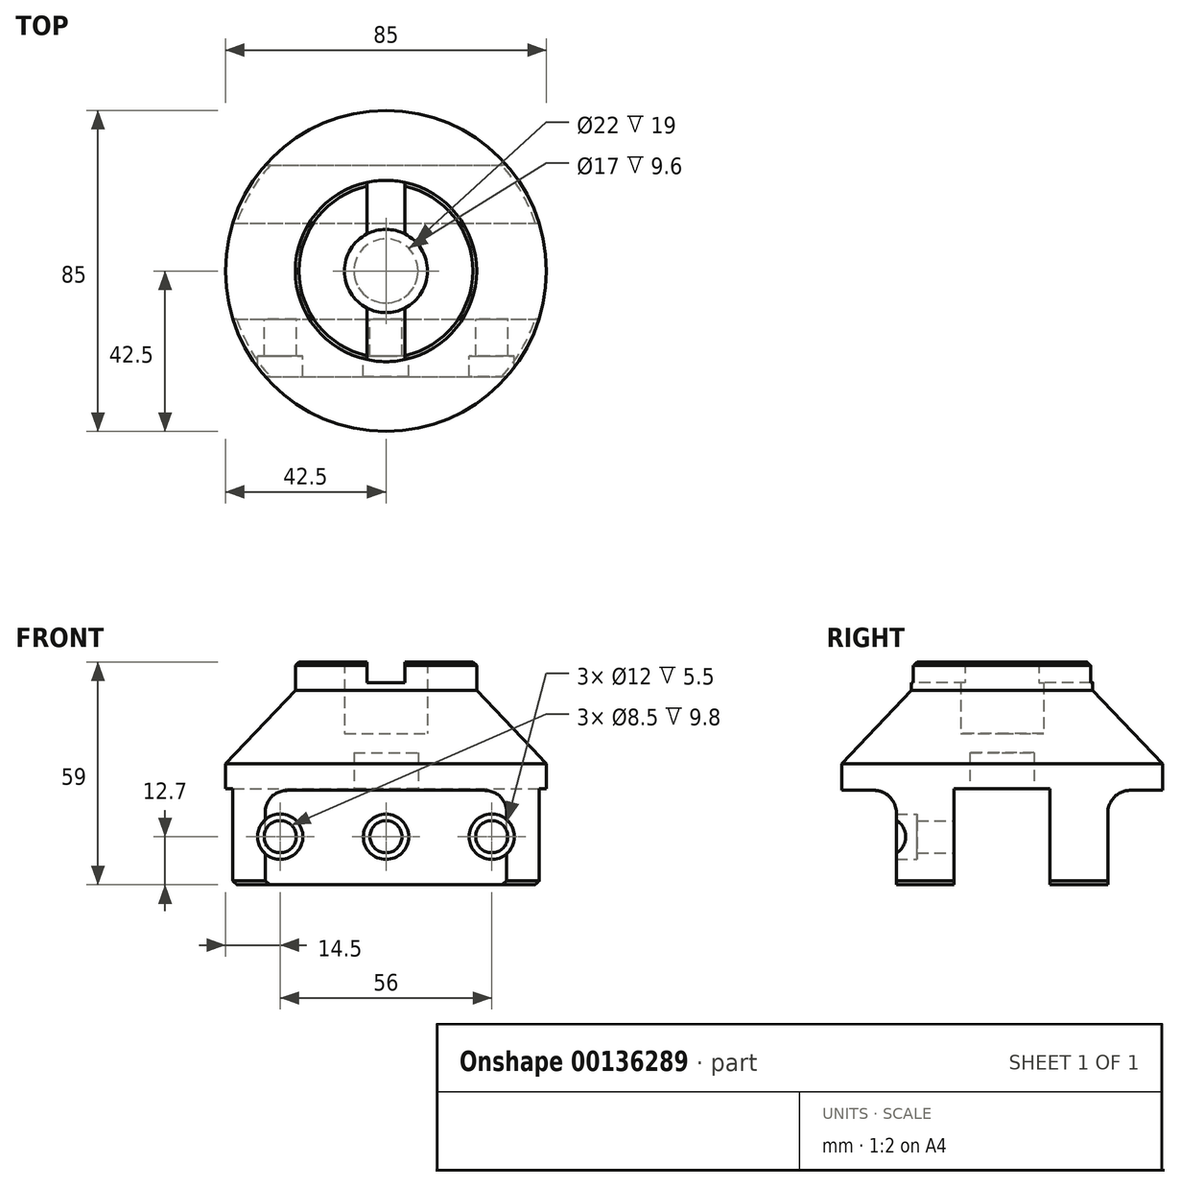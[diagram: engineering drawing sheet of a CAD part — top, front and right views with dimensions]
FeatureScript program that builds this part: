
annotation { "Feature Type Name" : "Feature", "Feature Type Description" : "" }
export const myFeature = defineFeature(function(context is Context, id is Id, definition is map)
    precondition{}
    {
        {
            var Q0;
            Q0=qCreatedBy(makeId("Front.planeOp"),FACE);
            var sketch = newSketch(context, id + "F0", { "sketchPlane" : qUnion([Q0])});
            skLineSegment(sketch, "E0", {"start": v(0, 0) * mm, "end": v(42.5, 0) * mm});
            skLineSegment(sketch, "E1", {"start": v(42.5, 0) * mm, "end": v(42.5, 32) * mm});
            skLineSegment(sketch, "E2", {"start": v(42.5, 32) * mm, "end": v(24, 51.5) * mm});
            skLineSegment(sketch, "E3", {"start": v(24, 51.5) * mm, "end": v(24, 59) * mm});
            skLineSegment(sketch, "E4", {"start": v(24, 59) * mm, "end": v(0, 59) * mm});
            skLineSegment(sketch, "E5", {"start": v(0, 59) * mm, "end": v(0, 0) * mm});
            skSolve(sketch);
        }
        {
            var Q0;
            Q0=makeQuery(id+"F0.imprint","IMPRINT",FACE,{"disambiguationData":[TD([[makeQuery(id+"F0.imprint","IMPRINT",EDGE,{"derivedFrom":sQuery(id+"F0.wireOp",EDGE,"E0")}),1.0]])]});
            var Q1;
            Q1=sQuery(id+"F0.wireOp",EDGE,"E5");
            revolve(context, id + "F1", {"entities" : qUnion([Q0]), "axis" : qUnion([Q1]), "revolveType" : RevolveType.FULL});
        }
        {
            var Q0;
            Q0=qCreatedBy(makeId("Front.planeOp"),FACE);
            var sketch = newSketch(context, id + "F2", { "sketchPlane" : qUnion([Q0])});
            skLineSegment(sketch, "E6.bottom", {"start": v(0, 59) * mm, "end": v(11, 59) * mm});
            skLineSegment(sketch, "E6.top", {"start": v(0, 40) * mm, "end": v(11, 40) * mm});
            skLineSegment(sketch, "E6.left", {"start": v(0, 59) * mm, "end": v(0, 40) * mm});
            skLineSegment(sketch, "E6.right", {"start": v(11, 59) * mm, "end": v(11, 40) * mm});
            skPoint(sketch, "E7.oppositeSnap0", {"position": v(5.5, 40) * mm});
            skLineSegment(sketch, "E7.bottom", {"start": v(0, 40) * mm, "end": v(5.5, 40) * mm});
            skLineSegment(sketch, "E7.top", {"start": v(0, 35) * mm, "end": v(5.5, 35) * mm});
            skLineSegment(sketch, "E7.left", {"start": v(0, 40) * mm, "end": v(0, 35) * mm});
            skLineSegment(sketch, "E7.right", {"start": v(5.5, 40) * mm, "end": v(5.5, 35) * mm});
            skLineSegment(sketch, "E8.bottom", {"start": v(0, 35) * mm, "end": v(8.5, 35) * mm});
            skLineSegment(sketch, "E8.top", {"start": v(0, 25) * mm, "end": v(8.5, 25) * mm});
            skLineSegment(sketch, "E8.left", {"start": v(0, 35) * mm, "end": v(0, 25) * mm});
            skLineSegment(sketch, "E8.right", {"start": v(8.5, 35) * mm, "end": v(8.5, 25) * mm});
            skSolve(sketch);
        }
        {
            var Q0;
            Q0=makeQuery(id+"F2.imprint","IMPRINT",FACE,{"disambiguationData":[TD([[makeQuery(id+"F2.imprint","IMPRINT",EDGE,{"derivedFrom":sQuery(id+"F2.wireOp",EDGE,"E8.top")}),1.0]])]});
            var Q1;
            Q1=makeQuery(id+"F2.imprint","IMPRINT",FACE,{"disambiguationData":[TD([[makeQuery(id+"F2.imprint","IMPRINT",EDGE,{"derivedFrom":sQuery(id+"F2.wireOp",EDGE,"E7.bottom")}),-1.0]])]});
            var Q2;
            Q2=makeQuery(id+"F2.imprint","IMPRINT",FACE,{"disambiguationData":[TD([[makeQuery(id+"F2.imprint","IMPRINT",EDGE,{"derivedFrom":sQuery(id+"F2.wireOp",EDGE,"E6.bottom")}),-1.0]])]});
            var Q3;
            Q3=sQuery(id+"F2.wireOp",EDGE,"E8.left");
            revolve(context, id + "F3", {"operationType" : NewBodyOperationType.REMOVE, "entities" : qUnion([Q0, Q1, Q2]), "axis" : qUnion([Q3]), "revolveType" : RevolveType.FULL, "oppositeDirection" : true});
        }
        {
            var Q0;
            Q0=qCreatedBy(makeId("Right.planeOp"),FACE);
            var sketch = newSketch(context, id + "F4", { "sketchPlane" : qUnion([Q0])});
            skLineSegment(sketch, "E9.bottom", {"start": v(12.7, 25.4) * mm, "end": v(-12.7, 25.4) * mm});
            skLineSegment(sketch, "E9.top", {"start": v(12.7, 0) * mm, "end": v(-12.7, 0) * mm});
            skLineSegment(sketch, "E9.left", {"start": v(12.7, 25.4) * mm, "end": v(12.7, 0) * mm});
            skLineSegment(sketch, "E9.right", {"start": v(-12.7, 25.4) * mm, "end": v(-12.7, 0) * mm});
            skSolve(sketch);
        }
        {
            var Q0;
            Q0 = qSketchRegion(id + "F4", true);
            extrude(context, id + "F5", {"entities" : qUnion([Q0]), "operationType" : NewBodyOperationType.REMOVE, "endBound" : BoundingType.SYMMETRIC, "oppositeDirection" : true, "depth" : 100 * mm});
        }
        {
            var Q0;
            Q0=qCreatedBy(makeId("Front.planeOp"),FACE);
            var sketch = newSketch(context, id + "F6", { "sketchPlane" : qUnion([Q0])});
            skLineSegment(sketch, "E10.bottom", {"start": v(-5, 59) * mm, "end": v(5, 59) * mm});
            skLineSegment(sketch, "E10.top", {"start": v(-5, 53.5) * mm, "end": v(5, 53.5) * mm});
            skLineSegment(sketch, "E10.left", {"start": v(-5, 59) * mm, "end": v(-5, 53.5) * mm});
            skLineSegment(sketch, "E10.right", {"start": v(5, 59) * mm, "end": v(5, 53.5) * mm});
            skSolve(sketch);
        }
        {
            var Q0;
            Q0 = qSketchRegion(id + "F6", true);
            extrude(context, id + "F7", {"entities" : qUnion([Q0]), "operationType" : NewBodyOperationType.REMOVE, "endBound" : BoundingType.SYMMETRIC, "oppositeDirection" : true, "depth" : 50 * mm});
        }
        {
            var Q0;
            Q0=qCreatedBy(makeId("Front.planeOp"),FACE);
            var sketch = newSketch(context, id + "F8", { "sketchPlane" : qUnion([Q0])});
            skCircle(sketch, "E11", {"center": v(0, 12.7) * mm, "radius": 4.25 * mm});
            skCircle(sketch, "E12", {"center": v(28, 12.7) * mm, "radius": 4.25 * mm});
            skCircle(sketch, "E13.MirrorC", {"center": v(-28, 12.7) * mm, "radius": 4.25 * mm});
            skSolve(sketch);
        }
        {
            var Q0;
            Q0 = qSketchRegion(id + "F8", true);
            extrude(context, id + "F9", {"entities" : qUnion([Q0]), "operationType" : NewBodyOperationType.REMOVE, "depth" : 50 * mm});
        }
        {
            var Q0;
            {var subQ0=sQuery(id+"F0.wireOp",EDGE,"E0");var subQ1=sQuery(id+"F0.wireOp",EDGE,"E1");Q0=makeQuery(id+"F5.boolean.opBoolean","SPLIT",EDGE,{"disambiguationData":[TD([makeQuery(id+"F5.opExtrude","SWEPT_FACE",FACE,{"disambiguationData":[OSD([sQuery(id+"F4.wireOp",EDGE,"E9.right")])]})])],"derivedFrom":makeQuery(id+"F1.opRevolve","SWEPT_EDGE",EDGE,{"disambiguationData":[OSD([subQ0,subQ1])]})});}
            var Q1;
            {var subQ0=sQuery(id+"F0.wireOp",EDGE,"E0");var subQ1=sQuery(id+"F0.wireOp",EDGE,"E1");Q1=makeQuery(id+"F5.boolean.opBoolean","SPLIT",EDGE,{"disambiguationData":[TD([makeQuery(id+"F5.opExtrude","SWEPT_FACE",FACE,{"disambiguationData":[OSD([sQuery(id+"F4.wireOp",EDGE,"E9.left")])]})])],"derivedFrom":makeQuery(id+"F1.opRevolve","SWEPT_EDGE",EDGE,{"disambiguationData":[OSD([subQ0,subQ1])]})});}
            var Q2;
            {var subQ0=sQuery(id+"F0.wireOp",EDGE,"E3");var subQ1=sQuery(id+"F0.wireOp",EDGE,"E4");Q2=makeQuery(id+"F7.boolean.opBoolean","SPLIT",EDGE,{"disambiguationData":[TD([makeQuery(id+"F7.opExtrude","SWEPT_FACE",FACE,{"disambiguationData":[OSD([sQuery(id+"F6.wireOp",EDGE,"E10.left")])]})])],"derivedFrom":makeQuery(id+"F1.opRevolve","SWEPT_EDGE",EDGE,{"disambiguationData":[OSD([subQ0,subQ1])]})});}
            var Q3;
            {var subQ0=sQuery(id+"F0.wireOp",EDGE,"E3");var subQ1=sQuery(id+"F0.wireOp",EDGE,"E4");Q3=makeQuery(id+"F7.boolean.opBoolean","SPLIT",EDGE,{"disambiguationData":[TD([makeQuery(id+"F7.opExtrude","SWEPT_FACE",FACE,{"disambiguationData":[OSD([sQuery(id+"F6.wireOp",EDGE,"E10.right")])]})])],"derivedFrom":makeQuery(id+"F1.opRevolve","SWEPT_EDGE",EDGE,{"disambiguationData":[OSD([subQ0,subQ1])]})});}
            chamfer(context, id + "F10", {"entities" : qUnion([Q0, Q1, Q2, Q3]), "width" : 1 * mm, "tangentPropagation" : true});
        }
        {
            var Q0;
            Q0=qCreatedBy(makeId("Front.planeOp"),FACE);
            cPlane(context, id + "F11", {"entities" : qUnion([Q0]), "cplaneType" : CPlaneType.OFFSET, "offset" : 22.5 * mm, "width" : 150 * mm, "height" : 150 * mm});
        }
        {
            var Q0;
            Q0=qCreatedBy(id+"F11.planeOp",FACE);
            var sketch = newSketch(context, id + "F12", { "sketchPlane" : qUnion([Q0])});
            skCircle(sketch, "E14", {"center": v(0, 12.7) * mm, "radius": 6 * mm});
            skCircle(sketch, "E15", {"center": v(-28, 12.7) * mm, "radius": 6 * mm});
            skCircle(sketch, "E16.MirrorC", {"center": v(28, 12.7) * mm, "radius": 6 * mm});
            skSolve(sketch);
        }
        {
            var Q0;
            Q0 = qSketchRegion(id + "F12", true);
            extrude(context, id + "F13", {"entities" : qUnion([Q0]), "operationType" : NewBodyOperationType.REMOVE, "depth" : 25 * mm});
        }
        {
            var Q0;
            Q0=qCreatedBy(makeId("Right.planeOp"),FACE);
            var sketch = newSketch(context, id + "F14", { "sketchPlane" : qUnion([Q0])});
            skLineSegment(sketch, "E17.bottom", {"start": v(-49.66, 25) * mm, "end": v(-34, 25) * mm});
            skLineSegment(sketch, "E17.top", {"start": v(-49.66, -7.6) * mm, "end": v(-28, -7.6) * mm});
            skLineSegment(sketch, "E17.left", {"start": v(-49.66, 25) * mm, "end": v(-49.66, -7.6) * mm});
            skLineSegment(sketch, "E17.right", {"start": v(-28, 19) * mm, "end": v(-28, -7.6) * mm});
            skLineSegment(sketch, "E18.MirrorCS", {"start": v(49.66, 25) * mm, "end": v(49.66, -7.6) * mm});
            skLineSegment(sketch, "E19.MirrorCS", {"start": v(49.66, -7.6) * mm, "end": v(28, -7.6) * mm});
            skLineSegment(sketch, "E20.MirrorCS", {"start": v(28, 19) * mm, "end": v(28, -7.6) * mm});
            skLineSegment(sketch, "E21.MirrorCS", {"start": v(49.66, 25) * mm, "end": v(34, 25) * mm});
            skPoint(sketch, "E22.visualSharp", {"position": v(-28, 25) * mm});
            skArc(sketch, "E22.filletArc", {"start": v(-28, 19) * mm, "mid": v(-29.76, 23.24) * mm, "end": v(-34, 25) * mm});
            skPoint(sketch, "E23.visualSharp", {"position": v(28, 25) * mm});
            skArc(sketch, "E23.filletArc", {"start": v(34, 25) * mm, "mid": v(29.76, 23.24) * mm, "end": v(28, 19) * mm});
            skSolve(sketch);
        }
        {
            var Q0;
            Q0 = qSketchRegion(id + "F14", true);
            extrude(context, id + "F15", {"entities" : qUnion([Q0]), "operationType" : NewBodyOperationType.REMOVE, "endBound" : BoundingType.SYMMETRIC, "oppositeDirection" : true, "depth" : 80 * mm});
        }
    });
